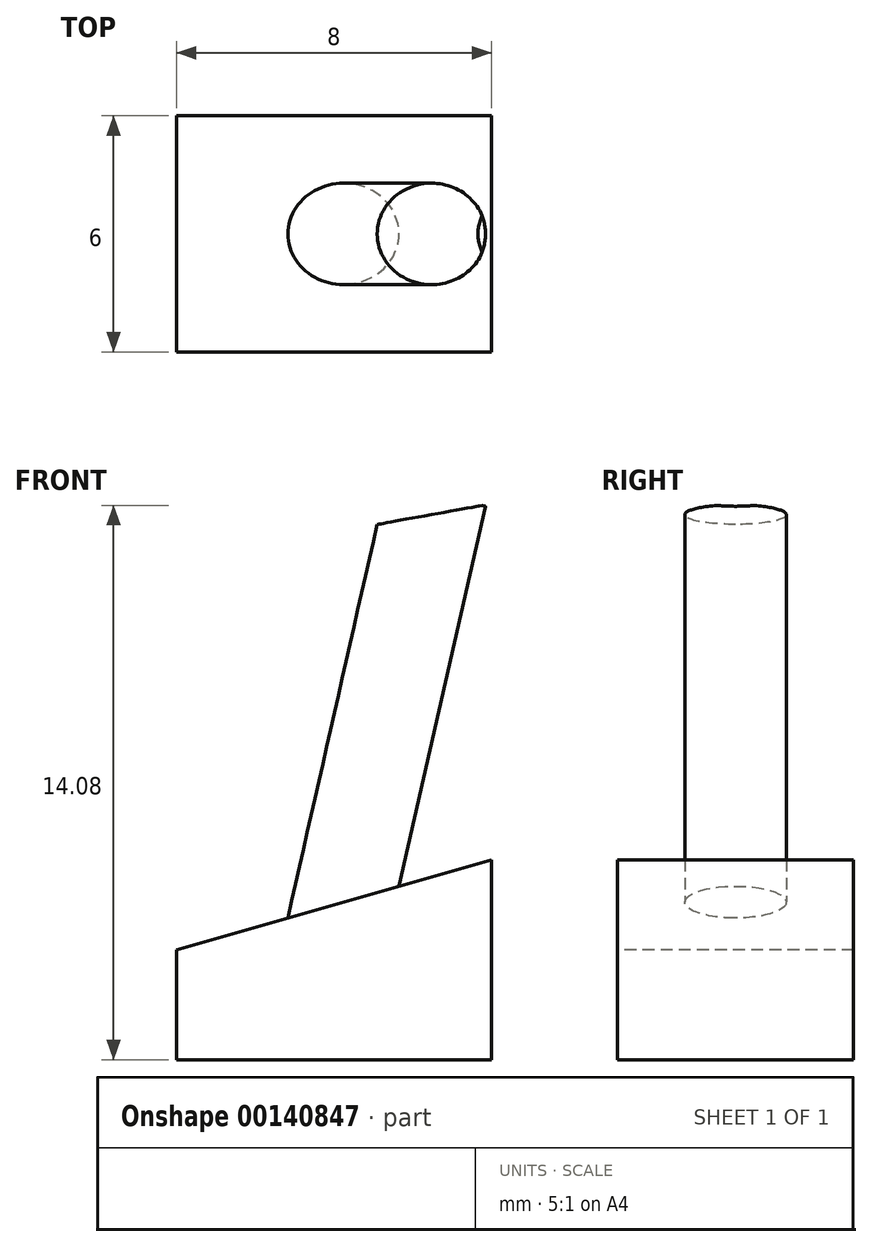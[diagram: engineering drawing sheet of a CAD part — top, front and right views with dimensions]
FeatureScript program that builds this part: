
annotation { "Feature Type Name" : "Feature", "Feature Type Description" : "" }
export const myFeature = defineFeature(function(context is Context, id is Id, definition is map)
    precondition{}
    {
        {
            var Q0;
            Q0=qCreatedBy(makeId("Top.planeOp"),FACE);
            var sketch = newSketch(context, id + "F0", { "sketchPlane" : qUnion([Q0])});
            skLineSegment(sketch, "E0.bottom", {"start": v(-4, 3) * mm, "end": v(4, 3) * mm});
            skLineSegment(sketch, "E0.top", {"start": v(-4, -3) * mm, "end": v(4, -3) * mm});
            skLineSegment(sketch, "E0.left", {"start": v(-4, 3) * mm, "end": v(-4, -3) * mm});
            skLineSegment(sketch, "E0.right", {"start": v(4, 3) * mm, "end": v(4, -3) * mm});
            skPoint(sketch, "E0.middle", {"position": v(0, 0) * mm});
            skSolve(sketch);
        }
        {
            var Q0;
            Q0 = qSketchRegion(id + "F0", true);
            extrude(context, id + "F1", {"entities" : qUnion([Q0]), "depth" : 5.08 * mm, "offsetDistance" : 25.4 * mm});
        }
        {
            var Q0;
            Q0=makeQuery(id+"F1.opExtrude","SWEPT_FACE",FACE,{"disambiguationData":[OSD([sQuery(id+"F0.wireOp",EDGE,"E0.top")])]});
            var sketch = newSketch(context, id + "F2", { "sketchPlane" : qUnion([Q0])});
            skLineSegment(sketch, "E1", {"start": v(4, 5.08) * mm, "end": v(-4, 2.8) * mm});
            skLineSegment(sketch, "E2", {"start": v(-4, 2.8) * mm, "end": v(-4, 5.08) * mm});
            skLineSegment(sketch, "E3", {"start": v(-4, 5.08) * mm, "end": v(4, 5.08) * mm});
            skSolve(sketch);
        }
        {
            var Q0;
            Q0=makeQuery(id+"F2.imprint","IMPRINT",FACE,{"disambiguationData":[TD([[makeQuery(id+"F2.imprint","IMPRINT",EDGE,{"derivedFrom":sQuery(id+"F2.wireOp",EDGE,"E1")}),-1.0]])]});
            extrude(context, id + "F3", {"entities" : qUnion([Q0]), "operationType" : NewBodyOperationType.REMOVE, "oppositeDirection" : true, "depth" : 25.4 * mm, "offsetDistance" : 25.4 * mm});
        }
        {
            var Q0;
            Q0=qCreatedBy(makeId("Front.planeOp"),FACE);
            var sketch = newSketch(context, id + "F4", { "sketchPlane" : qUnion([Q0])});
            skLineSegment(sketch, "E4", {"start": v(0, 2.94) * mm, "end": v(2.52, 14.06) * mm});
            skLineSegment(sketch, "E5", {"start": v(2.52, 14.06) * mm, "end": v(3.85, 14.06) * mm});
            skLineSegment(sketch, "E6", {"start": v(3.85, 14.06) * mm, "end": v(1.26, 2.66) * mm});
            skLineSegment(sketch, "E7", {"start": v(1.26, 2.66) * mm, "end": v(0, 2.94) * mm});
            skSolve(sketch);
        }
        {
            var Q0;
            Q0=makeQuery(id+"F4.imprint","IMPRINT",FACE,{"disambiguationData":[TD([[makeQuery(id+"F4.imprint","IMPRINT",EDGE,{"derivedFrom":sQuery(id+"F4.wireOp",EDGE,"E4")}),-1.0]])]});
            var Q1;
            Q1=sQuery(id+"F4.wireOp",EDGE,"E4");
            revolve(context, id + "F5", {"operationType" : NewBodyOperationType.ADD, "entities" : qUnion([Q0]), "axis" : qUnion([Q1]), "revolveType" : RevolveType.FULL});
        }
        {
            var Q0;
            Q0=qCreatedBy(makeId("Front.planeOp"),FACE);
            var sketch = newSketch(context, id + "F6", { "sketchPlane" : qUnion([Q0])});
            skLineSegment(sketch, "E8", {"start": v(-1.62, 13.1) * mm, "end": v(7.57, 14.76) * mm});
            skLineSegment(sketch, "E9", {"start": v(7.57, 14.76) * mm, "end": v(2.5, 17.22) * mm});
            skLineSegment(sketch, "E10", {"start": v(2.5, 17.22) * mm, "end": v(-1.62, 13.1) * mm});
            skSolve(sketch);
        }
        {
            var Q0;
            Q0=makeQuery(id+"F6.imprint","IMPRINT",FACE,{"disambiguationData":[TD([[makeQuery(id+"F6.imprint","IMPRINT",EDGE,{"derivedFrom":sQuery(id+"F6.wireOp",EDGE,"E8")}),1.0]])]});
            extrude(context, id + "F7", {"entities" : qUnion([Q0]), "operationType" : NewBodyOperationType.REMOVE, "endBound" : BoundingType.SYMMETRIC, "depth" : 25.4 * mm, "offsetDistance" : 25.4 * mm});
        }
    });
